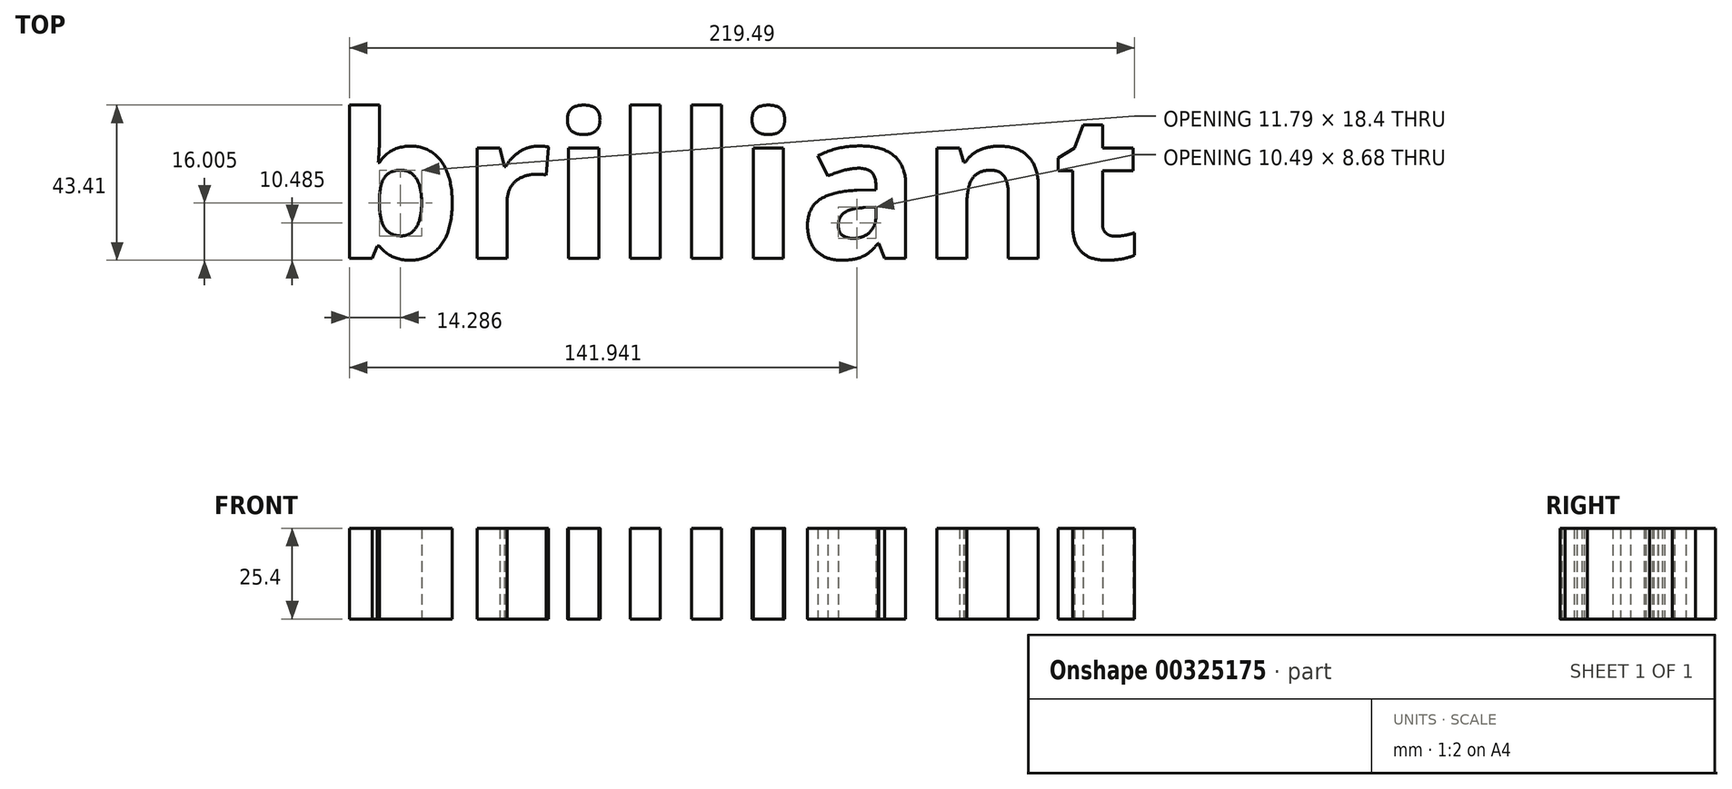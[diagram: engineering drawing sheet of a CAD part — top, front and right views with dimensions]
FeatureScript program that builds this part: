
annotation { "Feature Type Name" : "Feature", "Feature Type Description" : "" }
export const myFeature = defineFeature(function(context is Context, id is Id, definition is map)
    precondition{}
    {
        {
            var Q0;
            Q0=qCreatedBy(makeId("Top.planeOp"),FACE);
            var sketch = newSketch(context, id + "F0", { "sketchPlane" : qUnion([Q0])});
            skText(sketch, "E0", { "text": "brilliant", "fontName": "OpenSans-Bold.ttf"});
            const initialGuessF0  = {"E0": [-0.05204, -0.02461, 1, 0, 0.0406]};
            skSetInitialGuess(sketch, initialGuessF0);
            skSolve(sketch);
        }
        {
            var Q0;
            Q0 = qSketchRegion(id + "F0", true);
            extrude(context, id + "F1", {"entities" : qUnion([Q0]), "depth" : 25.4 * mm});
        }
    });
